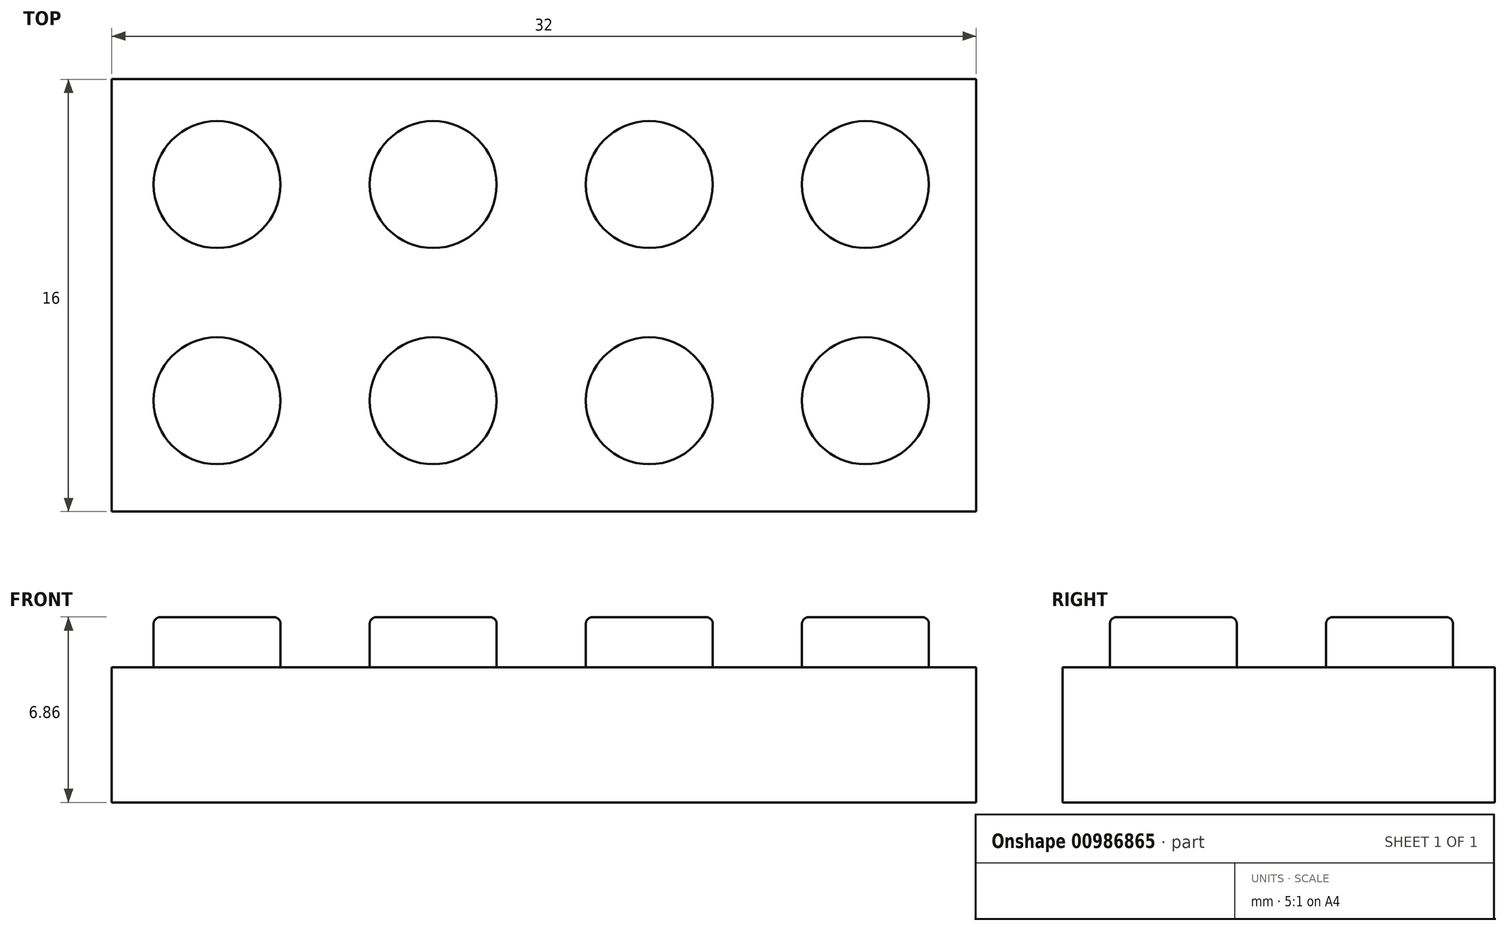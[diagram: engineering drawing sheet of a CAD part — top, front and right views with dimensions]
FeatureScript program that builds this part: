
annotation { "Feature Type Name" : "Feature", "Feature Type Description" : "" }
export const myFeature = defineFeature(function(context is Context, id is Id, definition is map)
    precondition{}
    {
        {
            var Q0;
            Q0=qCreatedBy(makeId("Top.planeOp"),FACE);
            var sketch = newSketch(context, id + "F0", { "sketchPlane" : qUnion([Q0])});
            skLineSegment(sketch, "E0.bottom", {"start": v(0, 0) * mm, "end": v(32, 0) * mm});
            skLineSegment(sketch, "E0.top", {"start": v(0, 16) * mm, "end": v(32, 16) * mm});
            skLineSegment(sketch, "E0.left", {"start": v(0, 0) * mm, "end": v(0, 16) * mm});
            skLineSegment(sketch, "E0.right", {"start": v(32, 0) * mm, "end": v(32, 16) * mm});
            skSolve(sketch);
        }
        {
            var Q0;
            Q0=makeQuery(id+"F0.imprint","IMPRINT",FACE,{"disambiguationData":[TD([[makeQuery(id+"F0.imprint","IMPRINT",EDGE,{"derivedFrom":sQuery(id+"F0.wireOp",EDGE,"E0.bottom")}),1.0]])]});
            extrude(context, id + "F1", {"entities" : qUnion([Q0]), "depth" : 5 * mm, "offsetDistance" : 25.4 * mm});
        }
        {
            var Q0;
            Q0=makeQuery(id+"F1.opExtrude","CAP_FACE",FACE,{"disambiguationData":[OSD([sQuery(id+"F0.wireOp",EDGE,"E0.bottom"),sQuery(id+"F0.wireOp",EDGE,"E0.top"),sQuery(id+"F0.wireOp",EDGE,"E0.left"),sQuery(id+"F0.wireOp",EDGE,"E0.right")])],"isStart":false});
            var sketch = newSketch(context, id + "F2", { "sketchPlane" : qUnion([Q0])});
            skCircle(sketch, "E1", {"center": v(3.9, 12.1) * mm, "radius": 2.35 * mm});
            skCircle(sketch, "E2.0.1.0", {"center": v(3.9, 4.1) * mm, "radius": 2.35 * mm});
            skCircle(sketch, "E2.1.0.0", {"center": v(11.9, 12.1) * mm, "radius": 2.35 * mm});
            skCircle(sketch, "E2.1.1.0", {"center": v(11.9, 4.1) * mm, "radius": 2.35 * mm});
            skCircle(sketch, "E2.2.0.0", {"center": v(19.9, 12.1) * mm, "radius": 2.35 * mm});
            skCircle(sketch, "E2.2.1.0", {"center": v(19.9, 4.1) * mm, "radius": 2.35 * mm});
            skCircle(sketch, "E2.3.0.0", {"center": v(27.9, 12.1) * mm, "radius": 2.35 * mm});
            skCircle(sketch, "E2.3.1.0", {"center": v(27.9, 4.1) * mm, "radius": 2.35 * mm});
            skLineSegment(sketch, "E2.direction1", {"start": v(3.9, 12.1) * mm, "end": v(11.9, 12.1) * mm, "construction": true});
            skLineSegment(sketch, "E2.direction2", {"start": v(3.9, 12.1) * mm, "end": v(3.9, 4.1) * mm, "construction": true});
            skSolve(sketch);
        }
        {
            var Q0;
            Q0=makeQuery(id+"F2.imprint","IMPRINT",FACE,{"disambiguationData":[TD([[makeQuery(id+"F2.imprint","IMPRINT",EDGE,{"derivedFrom":sQuery(id+"F2.wireOp",EDGE,"E2.0.1.0")}),1.0]])]});
            var Q1;
            Q1=makeQuery(id+"F2.imprint","IMPRINT",FACE,{"disambiguationData":[TD([[makeQuery(id+"F2.imprint","IMPRINT",EDGE,{"derivedFrom":sQuery(id+"F2.wireOp",EDGE,"E1")}),1.0]])]});
            var Q2;
            Q2=makeQuery(id+"F2.imprint","IMPRINT",FACE,{"disambiguationData":[TD([[makeQuery(id+"F2.imprint","IMPRINT",EDGE,{"derivedFrom":sQuery(id+"F2.wireOp",EDGE,"E2.1.0.0")}),1.0]])]});
            var Q3;
            Q3=makeQuery(id+"F2.imprint","IMPRINT",FACE,{"disambiguationData":[TD([[makeQuery(id+"F2.imprint","IMPRINT",EDGE,{"derivedFrom":sQuery(id+"F2.wireOp",EDGE,"E2.1.1.0")}),1.0]])]});
            var Q4;
            Q4=makeQuery(id+"F2.imprint","IMPRINT",FACE,{"disambiguationData":[TD([[makeQuery(id+"F2.imprint","IMPRINT",EDGE,{"derivedFrom":sQuery(id+"F2.wireOp",EDGE,"E2.2.1.0")}),1.0]])]});
            var Q5;
            Q5=makeQuery(id+"F2.imprint","IMPRINT",FACE,{"disambiguationData":[TD([[makeQuery(id+"F2.imprint","IMPRINT",EDGE,{"derivedFrom":sQuery(id+"F2.wireOp",EDGE,"E2.2.0.0")}),1.0]])]});
            var Q6;
            Q6=makeQuery(id+"F2.imprint","IMPRINT",FACE,{"disambiguationData":[TD([[makeQuery(id+"F2.imprint","IMPRINT",EDGE,{"derivedFrom":sQuery(id+"F2.wireOp",EDGE,"E2.3.0.0")}),1.0]])]});
            var Q7;
            Q7=makeQuery(id+"F2.imprint","IMPRINT",FACE,{"disambiguationData":[TD([[makeQuery(id+"F2.imprint","IMPRINT",EDGE,{"derivedFrom":sQuery(id+"F2.wireOp",EDGE,"E2.3.1.0")}),1.0]])]});
            extrude(context, id + "F3", {"entities" : qUnion([Q0, Q1, Q2, Q3, Q4, Q5, Q6, Q7]), "operationType" : NewBodyOperationType.ADD, "depth" : 1.85 * mm, "offsetDistance" : 25.4 * mm});
        }
        {
            var Q0;
            Q0=makeQuery(id+"F3.opExtrude","CAP_EDGE",EDGE,{"disambiguationData":[OSD([sQuery(id+"F2.wireOp",EDGE,"E2.0.1.0")])],"isStart":false});
            var Q1;
            Q1=makeQuery(id+"F3.opExtrude","CAP_EDGE",EDGE,{"disambiguationData":[OSD([sQuery(id+"F2.wireOp",EDGE,"E1")])],"isStart":false});
            var Q2;
            Q2=makeQuery(id+"F3.opExtrude","CAP_EDGE",EDGE,{"disambiguationData":[OSD([sQuery(id+"F2.wireOp",EDGE,"E2.1.1.0")])],"isStart":false});
            var Q3;
            Q3=makeQuery(id+"F3.opExtrude","CAP_EDGE",EDGE,{"disambiguationData":[OSD([sQuery(id+"F2.wireOp",EDGE,"E2.1.0.0")])],"isStart":false});
            var Q4;
            Q4=makeQuery(id+"F3.opExtrude","CAP_EDGE",EDGE,{"disambiguationData":[OSD([sQuery(id+"F2.wireOp",EDGE,"E2.2.1.0")])],"isStart":false});
            var Q5;
            Q5=makeQuery(id+"F3.opExtrude","CAP_EDGE",EDGE,{"disambiguationData":[OSD([sQuery(id+"F2.wireOp",EDGE,"E2.2.0.0")])],"isStart":false});
            var Q6;
            Q6=makeQuery(id+"F3.opExtrude","CAP_EDGE",EDGE,{"disambiguationData":[OSD([sQuery(id+"F2.wireOp",EDGE,"E2.3.0.0")])],"isStart":false});
            var Q7;
            Q7=makeQuery(id+"F3.opExtrude","CAP_EDGE",EDGE,{"disambiguationData":[OSD([sQuery(id+"F2.wireOp",EDGE,"E2.3.1.0")])],"isStart":false});
            fillet(context, id + "F4", {"entities" : qUnion([Q0, Q1, Q2, Q3, Q4, Q5, Q6, Q7]), "radius" : 0.25 * mm, "tangentPropagation" : true, "allowEdgeOverflow" : false});
        }
    });
